# Revit family: ARRN
name_source: partatom
category: Lighting Fixtures
revit_build: Autodesk Revit 2014 (Build: 20130308_1515(x64)
units: mm (PartAtom-declared; Revit-internal decimal feet)

## types (1)
- ARRN
    Apparent Load = 54 VA
    Assembly Code = D5020200
    Color Filter = 16777215
    Connector Description = Lighting Connector
    Default Elevation = 1219.2 mm  [stored 4 ft]
    Description = Sleek and highly efficient this reliable compact luminaire delivers a uniform photometric distribution and powerful performance of 130,000 maintenance free hours at 25°C . The excellent temperature range of -50°C to +55°C makes Arran a global lighting solution providing high output lighting at extreme temperatures. Offering an easily maintainable driver and LED strip, the Arran provides all the advantages of an LED luminaire with the benefit of extending its serviceable life.
    Dimming Lamp Color Temperature Shift = <None>
    Emit Shape Visible in Rendering = No
    Emit from Rectangle Length = 200 mm  [stored 0.656168 ft]
    Emit from Rectangle Width = 364 mm  [stored 1.19423 ft]
    Features = Instant on crisp white output.
Highly Energy Efficient.
Low temperature applications to -50°C.
130,000 maintenance free hours at 25°C.
    Fixture distribution = Direct
    Glass = Hubbell - Glass
    Height = 443 mm  [stored 1.45341 ft]
    Housing Material = Paint - Hubbell - Textured Camera Black
    IP Rating = IP66
    Lamp = LED
    Length = 444 mm  [stored 1.45669 ft]
    Load Classification = Lighting
    Manufacturer = Chalmit
    Model = ARRN
    Mounting = Paint - Hubbell - Light Silver
    Photometric Web File = ARRN_06L_LE.ies
    Power Factor = 1
    Product Documentation Link = https://hubbellcdn.com
    Product Link = https://www.hubbell.com
    Reflector Finish = Hubbell - White Glass
    Tilt Angle = 90.00°
    URL = https://www.hubbell.com
    Voltage = 120 V
    Warranty = 5 years Warranty
    Wattage Comments = 54
    Watts = 54 W
    Width = 136 mm
    Wings = Paint - Hubbell - Light Silver

note: [stored X ft] marks values corroborated as IEEE doubles in the binary element streams (Revit-internal decimal feet)

## geometry (parser evidence)
native form markers: Sweep x2
no freeform markers — native parametric forms only
